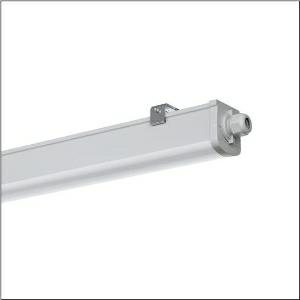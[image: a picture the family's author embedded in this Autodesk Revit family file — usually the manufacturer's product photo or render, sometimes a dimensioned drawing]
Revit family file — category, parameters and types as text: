
# Revit family: monsun_r__31_51fa207k430b_6f38
name_source: partatom
category: Lighting Fixtures
units: mm (PartAtom-declared; Revit-internal decimal feet)

## family parameters
Cut with Voids When Loaded = No
Host = Face
Light Source = No
Part Type = Normal
Room Calculation Point = No
Round Connector Dimension = Use Diameter
Shared = No

## types (1)
- Monsun® 31 (1 x LED, 3000 lm, 22 W, 4000K)
    Apparent Load = 22 VA
    CIE Flux Codes = 42 72 91 92 100
    Color Rendering = 80
    Color Temperature = 4000K
    Default Elevation = 1800 mm
    Description = Monsun® 31, damp-proof luminaire, primary optical cover: diffuser, of PC, frosted, light emission: direct distribution, primary light characteristic: symmetric, installation type: surface-mounted, LED, rated luminous flux: 3.000lm, luminous efficacy: 136lm/W, light colour: 840, colour temperature: 4000K, control gear: ON/OFF, with terminal, 3+1-pole, max. 2.5mm², through-wiring: 3x 2.5mm² + 1x 1.5mm², mains connection: 220..240V, AC, 50/60Hz, rated input power: 22W, housing, luminaire housing, of PC, light grey (RAL 7035), length: 1.158mm, width: 68mm, height: 76mm, protection rating (complete): IP66, insulation class (complete): insulation class II (safety insulation), certification: CE, ENEC, UKCA, protection symbol: D, impact resistance: IK08, permissible operating ambient temperature: -20..+40°C, corresponds to IFS (International Featured Standards) requirements for safety and quality in the food industry, contact your sales advisor before using the luminaires in applications with unclear chemical exposure, large temperature fluctuations or condensation-forming humidity, packaging unit: 1 piece
    Height = 77 mm
    Lamp = 1 x LED
    Lamp Light Flux = 3000 lm
    Lamp Power = 22 W
    Lamp count = 1
    Length = 1218 mm
    Luminous efficacy = 136 lm/W
    Manufacturer = Siteco
    ModVariant = No
    Model = 51FA207K430B
    Mounting Place = Ceiling
    Mounting Type = Surface mounted
    Number of Poles = 1
    OnlyDefault = Yes
    Power Factor = 1
    Product Name = Monsun® 31
    Product group = damp-proof luminaire
    ProductGroupID = 300
    Protection Class = Protection class II
    Protection Degree = IP 66
    RLX_Detail_Level = 1
    RLX_Emergency_Light_Flux = 0 lm
    RLX_Emergency_Type = 0
    RLX_Emergency_Type_DB = No
    RlxData = <blob elided: 32993 chars, md5=7b3ab975>
    Socket = socket
    Standby Power = 0 W
    System Light Flux = 3000 lm
    System Power = 22 W
    Type Comments = Product without accessories
    Type Image = l_1006174.jpg
    URL = http://relux.com
    VarID = ---
    Voltage = 0 V
    Weight = 0.00 kg
    Width = 69 mm

## geometry (parser evidence)
native form markers: Blend x4, Sweep x11
no freeform markers — native parametric forms only
